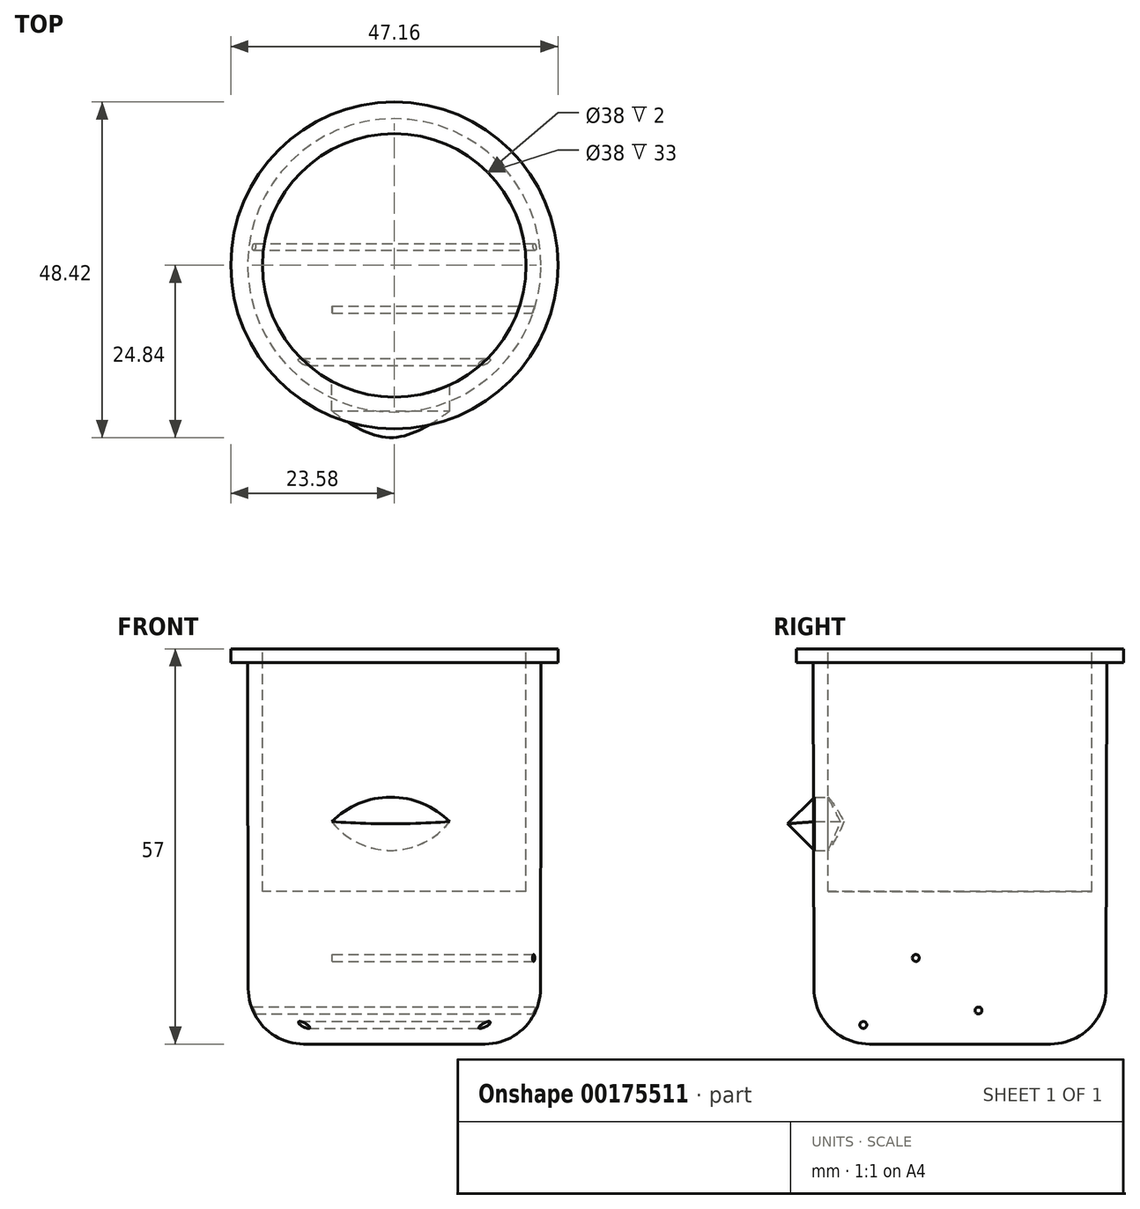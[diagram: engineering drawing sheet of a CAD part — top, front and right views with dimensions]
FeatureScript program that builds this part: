
annotation { "Feature Type Name" : "Feature", "Feature Type Description" : "" }
export const myFeature = defineFeature(function(context is Context, id is Id, definition is map)
    precondition{}
    {
        {
            var Q0;
            Q0=qCreatedBy(makeId("Top.planeOp"),FACE);
            cPlane(context, id + "F0", {"entities" : qUnion([Q0]), "cplaneType" : CPlaneType.OFFSET, "offset" : 55 * mm, "width" : 150 * mm, "height" : 150 * mm});
        }
        {
            var Q0;
            Q0=qCreatedBy(makeId("Top.planeOp"),FACE);
            var sketch = newSketch(context, id + "F1", { "sketchPlane" : qUnion([Q0])});
            skCircle(sketch, "E0", {"center": v(0, 0) * mm, "radius": 21.05 * mm});
            skSolve(sketch);
        }
        {
            var Q0;
            Q0=qCreatedBy(id+"F0.planeOp",FACE);
            var sketch = newSketch(context, id + "F2", { "sketchPlane" : qUnion([Q0])});
            skCircle(sketch, "E1", {"center": v(0, 0) * mm, "radius": 21.16 * mm});
            skSolve(sketch);
        }
        {
            var Q0;
            Q0=qSketchRegion(id+"F1",true);
            var Q1;
            Q1=qSketchRegion(id+"F2",true);
            loft(context, id + "F3", {"sheetProfilesArray" : [{ "sheetProfileEntities" : qUnion([Q0]) }, { "sheetProfileEntities" : qUnion([Q1]) }]});
        }
        {
            var Q0;
            Q0=makeQuery(id+"F3.opLoft","CAP_FACE",FACE,{"disambiguationData":[OSD([makeQuery(id+"F1.imprint","IMPRINT",FACE,{"disambiguationData":[TD([[makeQuery(id+"F1.imprint","IMPRINT",EDGE,{"derivedFrom":sQuery(id+"F1.wireOp",EDGE,"E0")}),1.0]])]})])],"isStart":true});
            fillet(context, id + "F4", {"entities" : qUnion([Q0]), "radius" : 8 * mm, "tangentPropagation" : true, "allowEdgeOverflow" : false});
        }
        {
            var Q0;
            Q0=qCreatedBy(makeId("Front.planeOp"),FACE);
            cPlane(context, id + "F5", {"entities" : qUnion([Q0]), "cplaneType" : CPlaneType.OFFSET, "offset" : 21 * mm, "width" : 150 * mm, "height" : 150 * mm});
        }
        {
            var Q0;
            Q0=qCreatedBy(id+"F5.planeOp",FACE);
            var sketch = newSketch(context, id + "F6", { "sketchPlane" : qUnion([Q0])});
            skLineSegment(sketch, "E2", {"start": v(0, 0) * mm, "end": v(0, 27.95) * mm});
            skArc(sketch, "E3", {"start": v(7.97, 32.08) * mm, "mid": v(-0.53, 35.62) * mm, "end": v(-9.03, 32.08) * mm});
            skArc(sketch, "E4", {"start": v(-9.03, 32.08) * mm, "mid": v(-0.53, 27.93) * mm, "end": v(7.97, 32.08) * mm});
            skSolve(sketch);
        }
        {
            var Q0;
            Q0=qSketchRegion(id+"F6",true);
            extrude(context, id + "F7", {"entities" : qUnion([Q0]), "endBound" : BoundingType.SYMMETRIC, "depth" : 10 * mm});
        }
        {
            var Q0;
            Q0=makeQuery(id+"F7.opExtrude","CAP_EDGE",EDGE,{"disambiguationData":[OSD([sQuery(id+"F6.wireOp",EDGE,"E3")])],"isStart":false});
            chamfer(context, id + "F8", {"entities" : qUnion([Q0]), "chamferType" : ChamferType.TWO_OFFSETS, "width1" : 5 * mm, "oppositeDirection" : false, "width2" : 5 * mm, "tangentPropagation" : true});
        }
        {
            var Q0;
            Q0=makeQuery(id+"F7.opExtrude","CAP_EDGE",EDGE,{"disambiguationData":[OSD([sQuery(id+"F6.wireOp",EDGE,"E4")])],"isStart":false});
            chamfer(context, id + "F9", {"entities" : qUnion([Q0]), "width" : 5 * mm, "tangentPropagation" : true});
        }
        {
            var Q0;
            Q0=qCreatedBy(id+"F0.planeOp",FACE);
            var sketch = newSketch(context, id + "F10", { "sketchPlane" : qUnion([Q0])});
            skCircle(sketch, "E5", {"center": v(0, 0) * mm, "radius": 23.58 * mm});
            skSolve(sketch);
        }
        {
            var Q0;
            Q0=qSketchRegion(id+"F10",true);
            extrude(context, id + "F11", {"entities" : qUnion([Q0]), "depth" : 2 * mm});
        }
        {
            var Q0;
            Q0=qCreatedBy(id+"F0.planeOp",FACE);
            cPlane(context, id + "F12", {"entities" : qUnion([Q0]), "cplaneType" : CPlaneType.OFFSET, "offset" : 2 * mm, "width" : 150 * mm, "height" : 150 * mm});
        }
        {
            var Q0;
            Q0=qCreatedBy(id+"F12.planeOp",FACE);
            var sketch = newSketch(context, id + "F13", { "sketchPlane" : qUnion([Q0])});
            skCircle(sketch, "E6", {"center": v(0, 0) * mm, "radius": 19 * mm});
            skSolve(sketch);
        }
        {
            var Q0;
            Q0=qSketchRegion(id+"F13",true);
            extrude(context, id + "F14", {"entities" : qUnion([Q0]), "operationType" : NewBodyOperationType.REMOVE, "oppositeDirection" : true, "depth" : 35 * mm});
        }
        {
            var Q0;
            Q0=qCreatedBy(makeId("Right.planeOp"),FACE);
            cPlane(context, id + "F15", {"entities" : qUnion([Q0]), "cplaneType" : CPlaneType.OFFSET, "offset" : 21 * mm, "width" : 150 * mm, "height" : 150 * mm});
        }
        {
            var Q0;
            Q0=qCreatedBy(id+"F15.planeOp",FACE);
            var sketch = newSketch(context, id + "F16", { "sketchPlane" : qUnion([Q0])});
            skLineSegment(sketch, "E7", {"start": v(2.66, 0) * mm, "end": v(2.66, 4.84) * mm});
            skCircle(sketch, "E8", {"center": v(2.66, 4.84) * mm, "radius": 0.5 * mm});
            skSolve(sketch);
        }
        {
            var Q0;
            Q0=qSketchRegion(id+"F16",true);
            extrude(context, id + "F17", {"entities" : qUnion([Q0]), "operationType" : NewBodyOperationType.REMOVE, "oppositeDirection" : true, "depth" : 58.07 * mm});
        }
        {
            var Q0;
            Q0=qCreatedBy(id+"F15.planeOp",FACE);
            var sketch = newSketch(context, id + "F18", { "sketchPlane" : qUnion([Q0])});
            skLineSegment(sketch, "E9", {"start": v(3.05, 4.76) * mm, "end": v(-13.95, 4.76) * mm});
            skLineSegment(sketch, "E10", {"start": v(-13.95, 4.76) * mm, "end": v(-13.95, 2.76) * mm});
            skCircle(sketch, "E11", {"center": v(-13.95, 2.76) * mm, "radius": 0.5 * mm});
            skSolve(sketch);
        }
        {
            var Q0;
            Q0=qSketchRegion(id+"F18",true);
            extrude(context, id + "F19", {"entities" : qUnion([Q0]), "operationType" : NewBodyOperationType.REMOVE, "oppositeDirection" : true, "depth" : 70 * mm});
        }
        {
            var Q0;
            Q0=qCreatedBy(id+"F15.planeOp",FACE);
            var sketch = newSketch(context, id + "F20", { "sketchPlane" : qUnion([Q0])});
            skLineSegment(sketch, "E12", {"start": v(-13.37, 2.86) * mm, "end": v(-6.37, 2.86) * mm});
            skLineSegment(sketch, "E13", {"start": v(-6.37, 2.86) * mm, "end": v(-6.37, 12.43) * mm});
            skCircle(sketch, "E14", {"center": v(-6.37, 12.43) * mm, "radius": 0.5 * mm});
            skSolve(sketch);
        }
        {
            var Q0;
            Q0=qSketchRegion(id+"F20",true);
            extrude(context, id + "F21", {"entities" : qUnion([Q0]), "operationType" : NewBodyOperationType.REMOVE, "oppositeDirection" : true, "depth" : 29.94 * mm});
        }
        {
            var Q0;
            Q0=qCreatedBy(makeId("Front.planeOp"),FACE);
            cPlane(context, id + "F22", {"entities" : qUnion([Q0]), "cplaneType" : CPlaneType.OFFSET, "offset" : 21 * mm, "oppositeDirection" : true, "width" : 150 * mm, "height" : 150 * mm});
        }
    });
